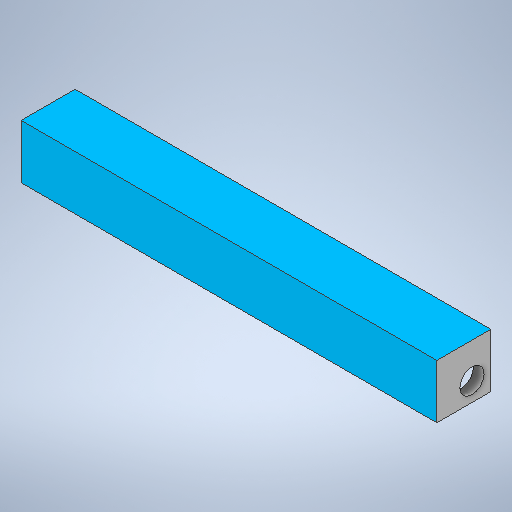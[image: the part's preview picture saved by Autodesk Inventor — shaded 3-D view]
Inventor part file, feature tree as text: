
AUTODESK INVENTOR PART (.ipt)
format: ipt  version: 2025.1 (Build 291241020, 241B)  size: 262,656 bytes
history: native  units: mm
features: sketch x4, extrude x4, hole x1
ambient origin geometry x8: Origin, YZ Plane, XZ Plane, XY Plane, X Axis, Y Axis, Z Axis, Center Point
bodies: Solid1 (feature_tree)
feature tree (9):
  sketch  "Sketch1"  dims[d1=10.0mm d3=2.0mm]
  extrude  "Extrusion1"  Depth=2.0mm
  extrude  "Extrusion2"  Depth=10.0mm TaperAngle=0.0deg
  extrude  "Extrusion3"  Depth=10.0mm
  extrude  "Extrusion4"  Depth=2.0mm TaperAngle=0.0deg
  hole  "Hole1"  [1 undecoded]
  sketch  "Sketch2"  dims[d4=2.0mm d5=0.0mm d6=10.0mm d7=0.0mm]
  sketch  "Sketch3"  dims[d8=10.0mm d9=10.0mm]
  sketch  "Sketch5"  dims[d10=2.0mm d11=0.0mm d12=2.0mm d13=0.0mm d19=77.0mm d23=3.5mm d24=3.5mm d25=4.5mm d26=6.0mm d27=9.4mm d28=2.0mm d29=90.0deg d30=8.0mm d31=20.594885mm]
note: 1 required parameter value undecoded (feature->parameter linkage not recoverable at this tier; creation-order binding heuristic only, values carry confidence <= 0.55)
